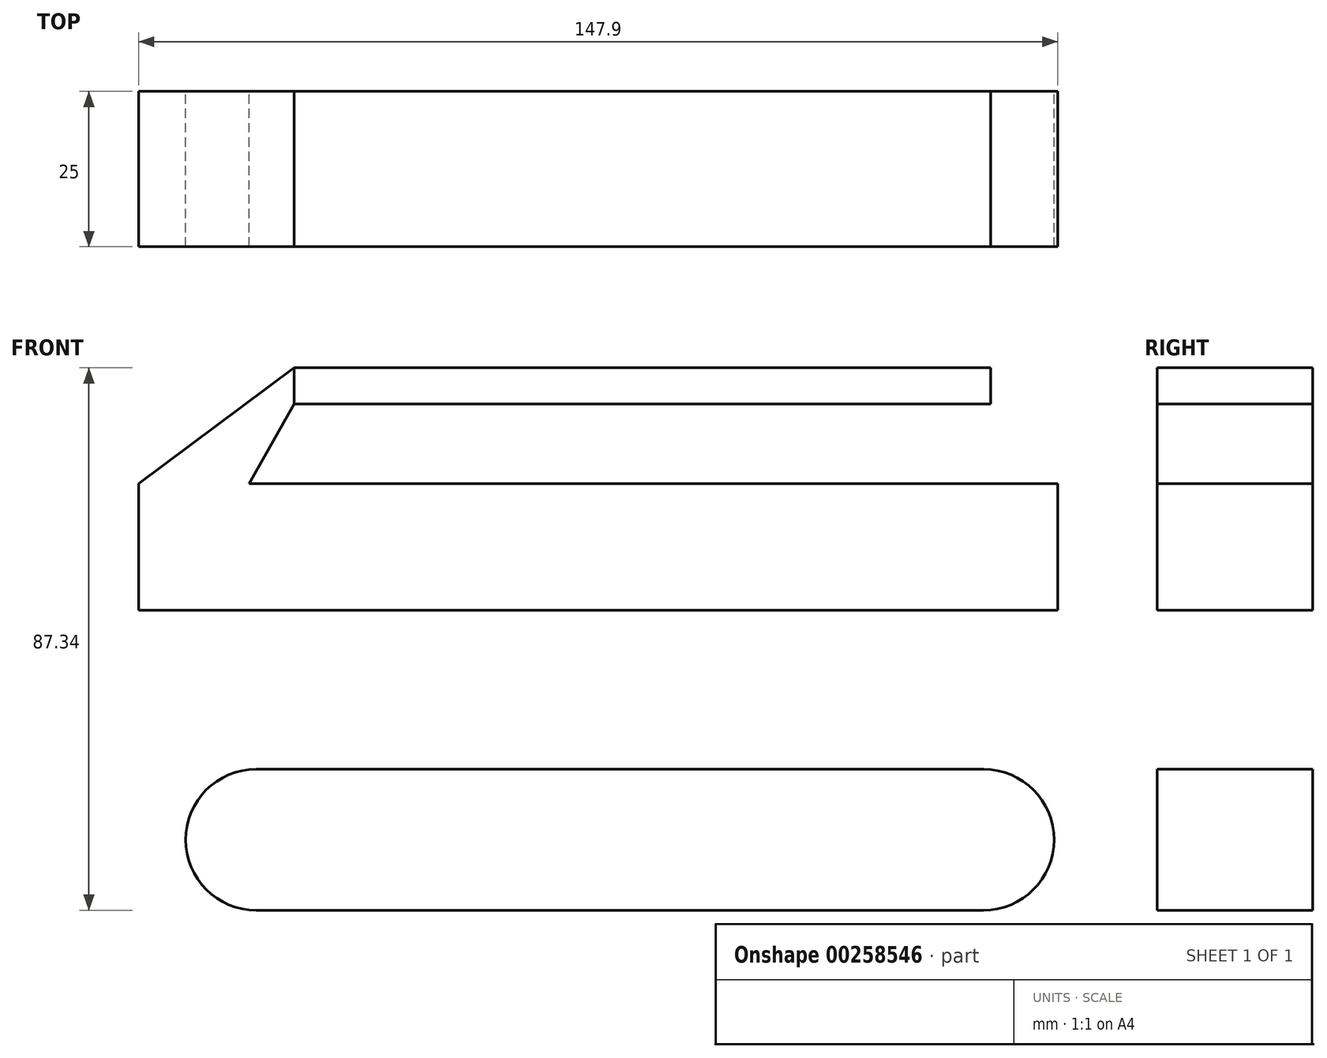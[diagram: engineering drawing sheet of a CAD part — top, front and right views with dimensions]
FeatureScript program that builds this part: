
annotation { "Feature Type Name" : "Feature", "Feature Type Description" : "" }
export const myFeature = defineFeature(function(context is Context, id is Id, definition is map)
    precondition{}
    {
        {
            var Q0;
            Q0=qCreatedBy(makeId("Front.planeOp"),FACE);
            var sketch = newSketch(context, id + "F0", { "sketchPlane" : qUnion([Q0])});
            skLineSegment(sketch, "E0.bottom", {"start": v(-49.78, -7.13) * mm, "end": v(67.25, -7.13) * mm});
            skLineSegment(sketch, "E0.top", {"start": v(-49.78, -29.84) * mm, "end": v(67.25, -29.84) * mm});
            skLineSegment(sketch, "E0.left", {"start": v(-49.78, -7.13) * mm, "end": v(-49.78, -29.84) * mm});
            skLineSegment(sketch, "E0.right", {"start": v(67.25, -7.13) * mm, "end": v(67.25, -29.84) * mm});
            skCircle(sketch, "E1", {"center": v(-49.78, -18.49) * mm, "radius": 11.35 * mm});
            skCircle(sketch, "E2", {"center": v(67.25, -18.49) * mm, "radius": 11.35 * mm});
            skLineSegment(sketch, "E3.bottom", {"start": v(-15.72, -7.13) * mm, "end": v(-20.38, -7.13) * mm});
            skLineSegment(sketch, "E3.top", {"start": v(-15.72, 10.34) * mm, "end": v(-20.38, 10.34) * mm});
            skLineSegment(sketch, "E3.left", {"start": v(-15.72, -7.13) * mm, "end": v(-15.72, 10.34) * mm});
            skLineSegment(sketch, "E3.right", {"start": v(-20.38, -7.13) * mm, "end": v(-20.38, 10.34) * mm});
            skLineSegment(sketch, "E4.bottom", {"start": v(-68.7, 38.87) * mm, "end": v(79.19, 38.87) * mm});
            skLineSegment(sketch, "E4.top", {"start": v(-68.7, 18.49) * mm, "end": v(79.19, 18.49) * mm});
            skLineSegment(sketch, "E4.left", {"start": v(-68.7, 38.87) * mm, "end": v(-68.7, 18.49) * mm});
            skLineSegment(sketch, "E4.right", {"start": v(79.19, 38.87) * mm, "end": v(79.19, 18.49) * mm});
            skLineSegment(sketch, "E5.bottom", {"start": v(-47.74, 18.49) * mm, "end": v(-43.67, 18.49) * mm});
            skLineSegment(sketch, "E5.top", {"start": v(-47.74, 2.47) * mm, "end": v(-43.67, 2.47) * mm});
            skLineSegment(sketch, "E5.left", {"start": v(-47.74, 18.49) * mm, "end": v(-47.74, 2.47) * mm});
            skLineSegment(sketch, "E5.right", {"start": v(-43.67, 18.49) * mm, "end": v(-43.67, 2.47) * mm});
            skLineSegment(sketch, "E6.bottom", {"start": v(79.19, 38.87) * mm, "end": v(68.41, 38.87) * mm});
            skLineSegment(sketch, "E6.top", {"start": v(79.19, 63.61) * mm, "end": v(68.41, 63.61) * mm});
            skLineSegment(sketch, "E6.left", {"start": v(79.19, 38.87) * mm, "end": v(79.19, 63.61) * mm});
            skLineSegment(sketch, "E6.right", {"start": v(68.41, 38.87) * mm, "end": v(68.41, 63.61) * mm});
            skLineSegment(sketch, "E7.bottom", {"start": v(68.41, 57.5) * mm, "end": v(-43.67, 57.5) * mm});
            skLineSegment(sketch, "E7.top", {"start": v(68.41, 51.68) * mm, "end": v(-43.67, 51.68) * mm});
            skLineSegment(sketch, "E7.left", {"start": v(68.41, 57.5) * mm, "end": v(68.41, 51.68) * mm});
            skLineSegment(sketch, "E7.right", {"start": v(-43.67, 57.5) * mm, "end": v(-43.67, 51.68) * mm});
            skLineSegment(sketch, "E8", {"start": v(-68.7, 38.87) * mm, "end": v(-43.67, 57.5) * mm});
            skLineSegment(sketch, "E9", {"start": v(-43.67, 51.68) * mm, "end": v(-50.95, 38.87) * mm});
            skSolve(sketch);
        }
        {
            var Q0;
            Q0=makeQuery(id+"F0.imprint","IMPRINT",FACE,{"disambiguationData":[TD([[makeQuery(id+"F0.imprint","IMPRINT",EDGE,{"derivedFrom":sQuery(id+"F0.wireOp",EDGE,"E7.bottom")}),1.0]])]});
            extrude(context, id + "F1", {"entities" : qUnion([Q0]), "depth" : 25 * mm});
        }
        {
            var Q0;
            Q0=makeQuery(id+"F0.imprint","IMPRINT",FACE,{"disambiguationData":[TD([[makeQuery(id+"F0.imprint","IMPRINT",EDGE,{"derivedFrom":sQuery(id+"F0.wireOp",EDGE,"E7.right")}),-1.0]])]});
            var Q1;
            {var subQ3=sQuery(id+"F0.wireOp",EDGE,"E4.left");Q1=makeQuery(id+"F0.imprint","IMPRINT",FACE,{"disambiguationData":[TD([[makeQuery(id+"F0.imprint","IMPRINT",EDGE,{"derivedFrom":subQ3}),1.0]])]});}
            var Q2;
            {var subQ1=sQuery(id+"F0.wireOp",EDGE,"E6.bottom");Q2=makeQuery(id+"F0.imprint","IMPRINT",FACE,{"disambiguationData":[TD([[makeQuery(id+"F0.imprint","IMPRINT",EDGE,{"derivedFrom":subQ1}),-1.0]])]});}
            var Q3;
            Q3=makeQuery(id+"F0.imprint","IMPRINT",FACE,{"disambiguationData":[TD([[makeQuery(id+"F0.imprint","IMPRINT",EDGE,{"derivedFrom":sQuery(id+"F0.wireOp",EDGE,"E5.bottom")}),-1.0]])]});
            extrude(context, id + "F2", {"entities" : qUnion([Q0, Q1, Q2, Q3]), "depth" : 25 * mm});
        }
        {
            var Q0;
            {var subQ4=sQuery(id+"F0.wireOp",EDGE,"E0.top");Q0=makeQuery(id+"F0.imprint","IMPRINT",FACE,{"disambiguationData":[TD([[makeQuery(id+"F0.imprint","IMPRINT",EDGE,{"derivedFrom":subQ4}),1.0]])]});}
            var Q1;
            Q1=makeQuery(id+"F0.imprint","IMPRINT",FACE,{"disambiguationData":[TD([[makeQuery(id+"F0.imprint","IMPRINT",EDGE,{"derivedFrom":sQuery(id+"F0.wireOp",EDGE,"E3.bottom")}),-1.0]])]});
            var Q2;
            {var subQ0=sQuery(id+"F0.wireOp",EDGE,"E0.left");Q2=makeQuery(id+"F0.imprint","IMPRINT",FACE,{"disambiguationData":[TD([[makeQuery(id+"F0.imprint","IMPRINT",EDGE,{"derivedFrom":subQ0}),1.0]])]});}
            var Q3;
            {var subQ0=sQuery(id+"F0.wireOp",EDGE,"E0.left");Q3=makeQuery(id+"F0.imprint","IMPRINT",FACE,{"disambiguationData":[TD([[makeQuery(id+"F0.imprint","IMPRINT",EDGE,{"derivedFrom":subQ0}),-1.0]])]});}
            var Q4;
            {var subQ0=sQuery(id+"F0.wireOp",EDGE,"E0.right");Q4=makeQuery(id+"F0.imprint","IMPRINT",FACE,{"disambiguationData":[TD([[makeQuery(id+"F0.imprint","IMPRINT",EDGE,{"derivedFrom":subQ0}),-1.0]])]});}
            var Q5;
            {var subQ0=sQuery(id+"F0.wireOp",EDGE,"E0.right");Q5=makeQuery(id+"F0.imprint","IMPRINT",FACE,{"disambiguationData":[TD([[makeQuery(id+"F0.imprint","IMPRINT",EDGE,{"derivedFrom":subQ0}),1.0]])]});}
            extrude(context, id + "F3", {"entities" : qUnion([Q0, Q1, Q2, Q3, Q4, Q5]), "depth" : 25 * mm});
        }
    });
